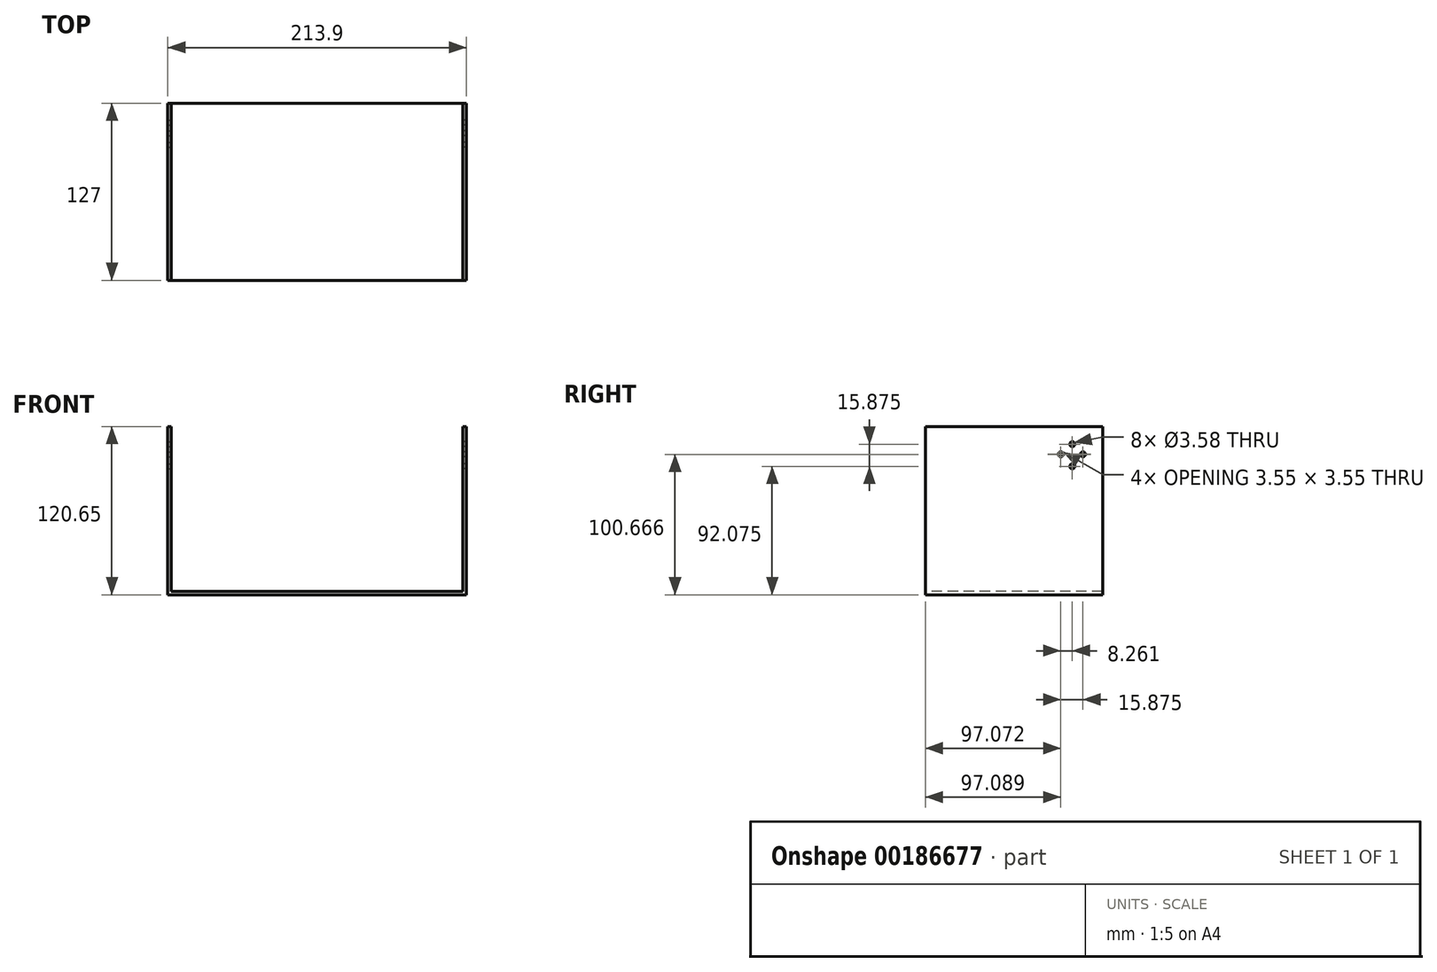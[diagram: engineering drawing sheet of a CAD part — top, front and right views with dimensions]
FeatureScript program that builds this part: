
annotation { "Feature Type Name" : "Feature", "Feature Type Description" : "" }
export const myFeature = defineFeature(function(context is Context, id is Id, definition is map)
    precondition{}
    {
        {
            var Q0;
            Q0=qCreatedBy(makeId("Top.planeOp"),FACE);
            var sketch = newSketch(context, id + "F0", { "sketchPlane" : qUnion([Q0])});
            skLineSegment(sketch, "E0.bottom", {"start": v(-106.95, 63.5) * mm, "end": v(106.95, 63.5) * mm});
            skLineSegment(sketch, "E0.top", {"start": v(-106.95, -63.5) * mm, "end": v(106.95, -63.5) * mm});
            skLineSegment(sketch, "E0.left", {"start": v(-106.95, 63.5) * mm, "end": v(-106.95, -63.5) * mm});
            skLineSegment(sketch, "E0.right", {"start": v(106.95, 63.5) * mm, "end": v(106.95, -63.5) * mm});
            skPoint(sketch, "E0.middle", {"position": v(0, 0) * mm});
            skSolve(sketch);
        }
        {
            var Q0;
            Q0 = qSketchRegion(id + "F0", true);
            extrude(context, id + "F1", {"entities" : qUnion([Q0]), "depth" : 120.65 * mm});
        }
        {
            var Q0;
            Q0=makeQuery(id+"F1.opExtrude","CAP_FACE",FACE,{"disambiguationData":[OSD([sQuery(id+"F0.wireOp",EDGE,"E0.bottom"),sQuery(id+"F0.wireOp",EDGE,"E0.top"),sQuery(id+"F0.wireOp",EDGE,"E0.left"),sQuery(id+"F0.wireOp",EDGE,"E0.right")])],"isStart":false});
            var sketch = newSketch(context, id + "F2", { "sketchPlane" : qUnion([Q0])});
            skLineSegment(sketch, "E1.bottom", {"start": v(-104.4, 63.5) * mm, "end": v(104.4, 63.5) * mm});
            skLineSegment(sketch, "E1.top", {"start": v(-104.4, -63.5) * mm, "end": v(104.4, -63.5) * mm});
            skLineSegment(sketch, "E1.left", {"start": v(-104.4, 63.5) * mm, "end": v(-104.4, -63.5) * mm});
            skLineSegment(sketch, "E1.right", {"start": v(104.4, 63.5) * mm, "end": v(104.4, -63.5) * mm});
            skSolve(sketch);
        }
        {
            var Q0;
            Q0 = qSketchRegion(id + "F2", true);
            extrude(context, id + "F3", {"entities" : qUnion([Q0]), "operationType" : NewBodyOperationType.REMOVE, "oppositeDirection" : true, "depth" : 118.36 * mm});
        }
        {
            var Q0;
            Q0=makeQuery(id+"F3.boolean.opBoolean","COPY",FACE,{"derivedFrom":makeQuery(id+"F3.opExtrude","SWEPT_FACE",FACE,{"disambiguationData":[OSD([sQuery(id+"F2.wireOp",EDGE,"E1.left")])]})});
            var sketch = newSketch(context, id + "F4", { "sketchPlane" : qUnion([Q0])});
            skCircle(sketch, "E2", {"center": v(41.83, 107.95) * mm, "radius": 1.8 * mm});
            skCircle(sketch, "E3", {"center": v(41.83, 92.08) * mm, "radius": 1.8 * mm});
            skCircle(sketch, "E4", {"center": v(33.57, 100.68) * mm, "radius": 1.8 * mm});
            skCircle(sketch, "E5", {"center": v(49.45, 100.68) * mm, "radius": 1.8 * mm});
            skLineSegment(sketch, "E6", {"start": v(33.57, 100.68) * mm, "end": v(49.45, 100.68) * mm});
            skLineSegment(sketch, "E7", {"start": v(41.83, 107.95) * mm, "end": v(41.83, 92.08) * mm});
            skPoint(sketch, "E8", {"position": v(41.83, 100.68) * mm});
            skSolve(sketch);
        }
        {
            var Q0;
            Q0 = qSketchRegion(id + "F4", true);
            extrude(context, id + "F5", {"entities" : qUnion([Q0]), "operationType" : NewBodyOperationType.REMOVE, "depth" : 220.47 * mm});
        }
        {
            var Q0;
            Q0 = qSketchRegion(id + "F4", true);
            extrude(context, id + "F6", {"entities" : qUnion([Q0]), "operationType" : NewBodyOperationType.REMOVE, "oppositeDirection" : true, "depth" : 25.4 * mm});
        }
        {
            var Q0;
            Q0=makeQuery(id+"F3.boolean.opBoolean","COPY",FACE,{"derivedFrom":makeQuery(id+"F3.opExtrude","SWEPT_FACE",FACE,{"disambiguationData":[OSD([sQuery(id+"F2.wireOp",EDGE,"E1.left")])]})});
            var sketch = newSketch(context, id + "F7", { "sketchPlane" : qUnion([Q0])});
            skLineSegment(sketch, "E9", {"start": v(-63.5, 61.47) * mm, "end": v(63.5, 61.47) * mm});
            skSolve(sketch);
        }
        {
            var Q0;
            {var subQ2=sQuery(id+"F7.wireOp",EDGE,"vVHIAIcI-6wQe-wTTa-wMtk-CF4KH9k9XdJg");Q0=makeQuery(id+"F7.imprint","IMPRINT",FACE,{"disambiguationData":[TD([[makeQuery(id+"F7.imprint","IMPRINT",EDGE,{"derivedFrom":subQ2}),-1.0]])]});}
            var Q1;
            Q1=sQuery(id+"F7.wireOp",EDGE,"E9");
            cPlane(context, id + "F8", {"entities" : qUnion([Q0, Q1]), "cplaneType" : CPlaneType.LINE_ANGLE, "offset" : 25.4 * mm, "angle" : 0 * degree, "width" : 152.4 * mm, "height" : 152.4 * mm});
        }
    });
